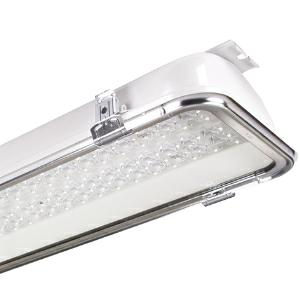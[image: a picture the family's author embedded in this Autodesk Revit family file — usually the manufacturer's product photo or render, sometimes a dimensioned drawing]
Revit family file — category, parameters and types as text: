
# Revit family: 3f_filippi_-_beta_235_76_vt_medio_3f_filippi_-_52555_-_beta_235_led_761x60_medio_vt_l1565
name_source: partatom
category: Lighting Fixtures
units: mm (PartAtom-declared; Revit-internal decimal feet)

## family parameters
Cut with Voids When Loaded = No
Host = Face
Light Source = No
Part Type = Normal
Room Calculation Point = No
Round Connector Dimension = Use Diameter
Shared = No

## types (1)
- 3F Filippi - Beta 235 76 VT Medio (1 x LED, 9861 lm, 65 W, 4000 K)
    Apparent Load = 65 VA
    Approval mark = CE
    CIE Flux Codes = 70 92 99 100 100
    Color Rendering = 80
    Color Temperature = 4000 K
    Control Gear = Electronic ballast
    Default Elevation = 1800 mm
    Description = ILLUMINOTECHNICAL
Luminous efficiency 100% (DLOR 100%, ULOR 0%).
Initial luminous flux of the luminaire 9861 lm.
Medium symmetric distribution.
Installation Interdistance Transv.D = 1.20 x hu - Long.D = 1.19 x hu.
Average luminance <3000 cd/m² for radial angles >65°.
Tabular UGR (CIE 117 - 4H-8H; S=0.25H; 70/50/20): RUG 18.9 - 19.6.
Beam angle: 76° - 75°.
Luminous efficacy 152 lm/W.
Lifetime (L93/B10): 30000 h. (tq+25°C)
Lifetime (L90/B10): 50000 h. (tq+25°C)
Lifetime (L85/B10): 80000 h. (tq+25°C)
Lifetime (L80/B10): 100000 h. (tq+25°C)
Lifetime (L85/B10): 50000 h. (tq+45°C)
Sudden decreased luminous flux after 50000 hours: 0% (C0).
Photobiological safety in compliance with IEC/TR 62778: RG0 risk exempt, (IEC 62471).
In compliance with IEC/EN 62722-2-1 - IEC/EN 62717 standards.

SOURCE
Linear LED module 60W/840.
Energy efficiency class (UE 2019/2020 - UE 2019/2015): C.
CIE 13.3 Colour rendering index: CRI >80 (R9 <50%).
IES TM-30 Fidelity Index: Rf = 84 Rg = 95.
CCT nominal colour temperature 4000 K.
Colour initial tolerance (MacAdam): SDCM 3.

MECHANICAL
Single-piece housing in pressed steel, powder-coated in white epoxy-polyester.
VT transparent glass, non-combustible, single-piece perimeter frame in galvanised steel.
Ecologic anti-aging injected sealing gasket.
Oversized gear-tray reflector unit in highly reflective white painted hot-galvanised steel.
Methacrylate (PMMA) lenses with external flat surface.
Galvanised steel snap-lock clips for diffuser mounting (safety n° 4 per fixture).
Luminaire with limited surface temperature. - D - (EN 60598-2-24)
Dimensions: 1565x235 mm, height 105 mm. Weight 11.45 kg.
IP66 protection degree.
Mechanical strength to impacts IK09 (10 joule).
Glow-wire test resistance 850°C.

ELECTRICAL
Halogen Free electronic wiring 230V-50/60Hz, power factor 0.95, THD <25%, constant output current, class I, 1 driver.
Power of the luminaire 65 W.
ENEC - CE.
Flicker: <4%.
Luminaire compliant with EN 60598-2-22 for power supply from a centralised emergency system CPSS (Central Power Supply System), not incorporated in the luminaire - high risk areas excluded. The default power and flux are 100% in AC and 100% in DC.
Ambient temperature from -20°C to +45°C.
Temperature class T6 max 85°C.
Quick connection via M20 3P connector with 9-13 mm tightening range.
Relative humidity UR: <85%.

INSTALLATION
Ceiling / Suspended / Wall.
All accessories dedicated to this product are available on the Catalog and on our website www.3F-Filippi.com.

APPLICATIONS
Dry, dusty indoor environments, subject to occasional water splashes.
Industrial environments, warehouses, environments where security locks are required on all clips, e.g. prisons (on request).
Environments in which it is necessary a total protection against falling fragments (eg environments with foodstuffs or machines with moving parts or with extreme temperature changes), use luminaires with laminated glass.
Tempered glass is not immune to falling fragments from harmless and caused by shocks or exceptionally derived from the tempering process.

WARNING
Fixture not suitable for cold stores with an ambient temperature <0°C and/or relative humidity >85%.
Luminaire designed for disposal/recycling at end-of-life.
Replaceable (LED only) light source by a professional. Replaceable control gear by a professional.
    Height = 105 mm
    Lamp = 1 x LED
    Lamp Light Flux = 9861 lm
    Lamp Power = 65 W
    Lamp count = 1
    Length = 1565 mm
    Lifetime = 50000 h
    Luminous efficacy = 152 lm/W
    Manufacturer = 3F Filippi
    ModVariant = No
    Model = 3F Filippi - 52555 - Beta 235 LED 761x60 MEDIO VT L1565
    Mounting Place = Ceiling
    Mounting Type = Pendant
    Number of Poles = 1
    OnlyDefault = Yes
    Power Factor = 1
    Product Name = 3F Filippi - Beta 235 76 VT Medio
    Product group = pendant luminaire
    ProductGroupID = 9
    Protection Class = Protection class I
    Protection Degree = IP 66
    RLX_Detail_Level = 1
    RLX_Emergency_Light_Flux = 0 lm
    RLX_Emergency_Type = 0
    RLX_Emergency_Type_DB = No
    RlxData = <blob elided: 90765 chars, md5=456261b9>
    Socket = socket
    Standby Power = 0 W
    System Light Flux = 9861 lm
    System Power = 65 W
    Type Comments = Product without accessories
    Type Image = 3ffilippi_beta_235_led_76_vt.jpg
    URL = http://relux.com
    VarID = ---
    Voltage = 0 V
    Weight = 0.00 kg
    Width = 235 mm

## geometry (parser evidence)
native form markers: Blend x4, Sweep x13
no freeform markers — native parametric forms only
